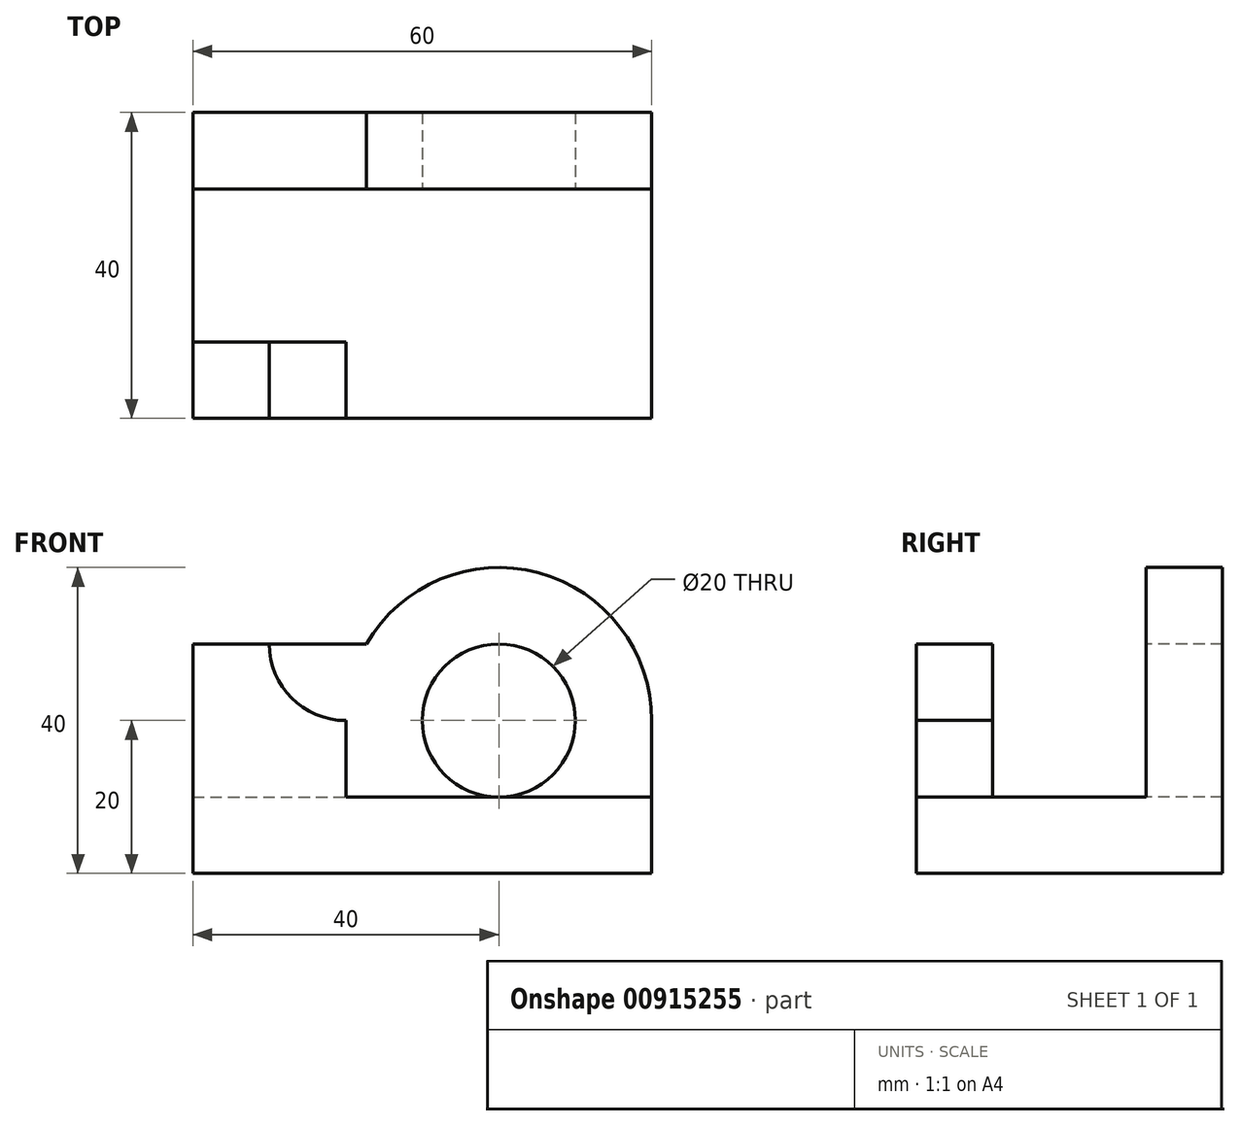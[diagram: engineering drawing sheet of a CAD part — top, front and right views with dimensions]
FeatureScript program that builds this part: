
annotation { "Feature Type Name" : "Feature", "Feature Type Description" : "" }
export const myFeature = defineFeature(function(context is Context, id is Id, definition is map)
    precondition{}
    {
        {
            var Q0;
            Q0=qCreatedBy(makeId("Top.planeOp"),FACE);
            var sketch = newSketch(context, id + "F0", { "sketchPlane" : qUnion([Q0])});
            skLineSegment(sketch, "E0.bottom", {"start": v(0, 0) * mm, "end": v(60, 0) * mm});
            skLineSegment(sketch, "E0.top", {"start": v(0, 40) * mm, "end": v(60, 40) * mm});
            skLineSegment(sketch, "E0.left", {"start": v(0, 0) * mm, "end": v(0, 40) * mm});
            skLineSegment(sketch, "E0.right", {"start": v(60, 0) * mm, "end": v(60, 40) * mm});
            skLineSegment(sketch, "E1", {"start": v(0, 30) * mm, "end": v(60, 30) * mm});
            skLineSegment(sketch, "E2", {"start": v(0, 10) * mm, "end": v(20, 10) * mm});
            skLineSegment(sketch, "E3", {"start": v(20, 10) * mm, "end": v(20, 0) * mm});
            skSolve(sketch);
        }
        {
            var Q0;
            {var subQ0=sQuery(id+"F0.wireOp",EDGE,"E1");Q0=makeQuery(id+"F0.imprint","IMPRINT",FACE,{"disambiguationData":[TD([[makeQuery(id+"F0.imprint","IMPRINT",EDGE,{"derivedFrom":subQ0}),-1.0]])]});}
            extrude(context, id + "F1", {"entities" : qUnion([Q0]), "depth" : 10 * mm, "offsetDistance" : 25 * mm});
        }
        {
            var Q0;
            {var subQ4=sQuery(id+"F0.wireOp",EDGE,"E2");Q0=makeQuery(id+"F0.imprint","IMPRINT",FACE,{"disambiguationData":[TD([[makeQuery(id+"F0.imprint","IMPRINT",EDGE,{"derivedFrom":subQ4}),-1.0]])]});}
            extrude(context, id + "F2", {"entities" : qUnion([Q0]), "operationType" : NewBodyOperationType.ADD, "depth" : 30 * mm, "offsetDistance" : 25 * mm});
        }
        {
            var Q0;
            {var subQ0=sQuery(id+"F0.wireOp",EDGE,"E0.top");Q0=makeQuery(id+"F0.imprint","IMPRINT",FACE,{"disambiguationData":[TD([[makeQuery(id+"F0.imprint","IMPRINT",EDGE,{"derivedFrom":subQ0}),-1.0]])]});}
            extrude(context, id + "F3", {"entities" : qUnion([Q0]), "operationType" : NewBodyOperationType.ADD, "depth" : 40 * mm, "offsetDistance" : 25 * mm});
        }
        {
            var Q0;
            {var subQ0=sQuery(id+"F0.wireOp",EDGE,"E0.bottom");Q0=makeQuery(id+"F2.boolean.opBoolean","MERGE",FACE,{"derivedFrom":[makeQuery(id+"F1.opExtrude","SWEPT_FACE",FACE,{"disambiguationData":[OSD([subQ0])]}),makeQuery(id+"F2.opExtrude","SWEPT_FACE",FACE,{"disambiguationData":[OSD([subQ0])]})]});}
            var sketch = newSketch(context, id + "F4", { "sketchPlane" : qUnion([Q0])});
            skArc(sketch, "E4", {"start": v(10, 30) * mm, "mid": v(12.93, 22.93) * mm, "end": v(20, 20) * mm});
            skSolve(sketch);
        }
        {
            var Q0;
            {var subQ0=sQuery(id+"F4.wireOp",EDGE,"E4");Q0=makeQuery(id+"F4.imprint","IMPRINT",FACE,{"disambiguationData":[TD([[makeQuery(id+"F4.imprint","IMPRINT",EDGE,{"derivedFrom":subQ0}),1.0]])]});}
            extrude(context, id + "F5", {"entities" : qUnion([Q0]), "operationType" : NewBodyOperationType.REMOVE, "endBound" : BoundingType.UP_TO_NEXT, "oppositeDirection" : true, "depth" : 25 * mm, "offsetDistance" : 25 * mm});
        }
        {
            var Q0;
            Q0=makeQuery(id+"F3.opExtrude","SWEPT_FACE",FACE,{"disambiguationData":[OSD([sQuery(id+"F0.wireOp",EDGE,"E1")])]});
            var sketch = newSketch(context, id + "F6", { "sketchPlane" : qUnion([Q0])});
            skArc(sketch, "E5", {"start": v(60, 20) * mm, "mid": v(45.18, 39.32) * mm, "end": v(22.68, 30) * mm});
            skCircle(sketch, "E6", {"center": v(40, 20) * mm, "radius": 10 * mm});
            skLineSegment(sketch, "E7.0", {"start": v(60, 40) * mm, "end": v(60, 10) * mm});
            skLineSegment(sketch, "E7.1", {"start": v(0, 40) * mm, "end": v(60, 40) * mm});
            skLineSegment(sketch, "E7.2", {"start": v(0, 40) * mm, "end": v(0, 10) * mm});
            skLineSegment(sketch, "E8", {"start": v(0, 30) * mm, "end": v(22.68, 30) * mm});
            skLineSegment(sketch, "E9.trimOffspring", {"start": v(57.32, 10) * mm, "end": v(60, 10) * mm});
            skPoint(sketch, "E10.0.start.orphan", {"position": v(20, 10) * mm});
            skSolve(sketch);
        }
        {
            var Q0;
            {var subQ0=sQuery(id+"F6.wireOp",EDGE,"E8");Q0=makeQuery(id+"F6.imprint","IMPRINT",FACE,{"disambiguationData":[TD([[makeQuery(id+"F6.imprint","IMPRINT",EDGE,{"derivedFrom":subQ0}),1.0]])]});}
            var Q1;
            {var subQ0=sQuery(id+"F6.wireOp",EDGE,"E7.0");var subQ1=sQuery(id+"F6.wireOp",EDGE,"E5");var subQ2=makeQuery(id+"F6.imprint","INTERSECT",VERTEX,{"derivedFrom":[subQ1,subQ0]});Q1=makeQuery(id+"F6.imprint","IMPRINT",FACE,{"disambiguationData":[TD([[makeQuery(id+"F6.imprint","IMPRINT",EDGE,{"disambiguationData":[TD([[subQ2,-1.0]])],"derivedFrom":subQ1}),-1.0]])]});}
            extrude(context, id + "F7", {"entities" : qUnion([Q0, Q1]), "operationType" : NewBodyOperationType.REMOVE, "endBound" : BoundingType.THROUGH_ALL, "oppositeDirection" : true, "depth" : 25 * mm, "offsetDistance" : 25 * mm});
        }
        {
            var Q0;
            Q0=makeQuery(id+"F6.imprint","IMPRINT",FACE,{"disambiguationData":[TD([[makeQuery(id+"F6.imprint","IMPRINT",EDGE,{"derivedFrom":sQuery(id+"F6.wireOp",EDGE,"E6")}),1.0]])]});
            extrude(context, id + "F8", {"entities" : qUnion([Q0]), "operationType" : NewBodyOperationType.REMOVE, "endBound" : BoundingType.THROUGH_ALL, "oppositeDirection" : true, "depth" : 25 * mm, "offsetDistance" : 25 * mm});
        }
    });
